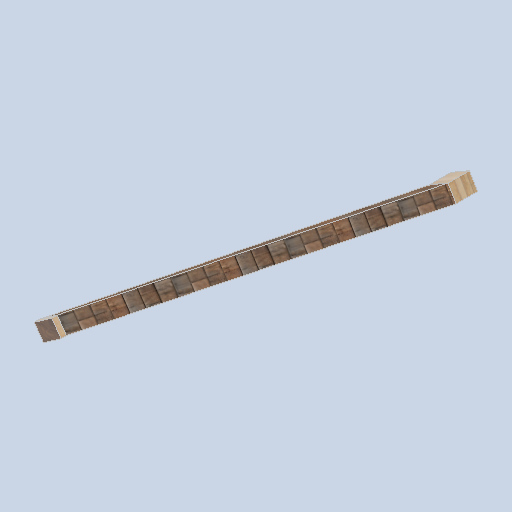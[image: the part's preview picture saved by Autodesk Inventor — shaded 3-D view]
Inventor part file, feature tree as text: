
AUTODESK INVENTOR PART (.ipt)
format: ipt  version: 2024.2 (Build 282272000, 272)  size: 318,464 bytes
history: native  units: mm
features: sketch x4, plane x2, extrude x2, loft x1, projected_geometry x1
ambient origin geometry x8: Origin, YZ Plane, XZ Plane, XY Plane, X Axis, Y Axis, Z Axis, Center Point
bodies: Solid1 (feature_tree)
feature tree (10):
  sketch  "Sketch5"  dims[d10=0.0mm d11=3749.0mm d12=0.0mm d13=90.0deg]
  plane  "Work Plane6"
  loft  "Loft1"
  extrude  "Extrusion1"  Depth=200.0mm TaperAngle=0.0deg
  extrude  "Extrusion2"  [1 undecoded]
  plane  "Work Plane5"
  sketch  "Sketch6"  dims[d14=0.0mm d15=90.0deg d16=200.0mm d17=0.0mm]
  sketch  "Sketch7"  dims[d18=50.0mm d19=0.0mm]
  sketch  "Sketch8"
  projected_geometry  "Projected Loop1"
note: 1 required parameter value undecoded (feature->parameter linkage not recoverable at this tier; creation-order binding heuristic only, values carry confidence <= 0.55)
